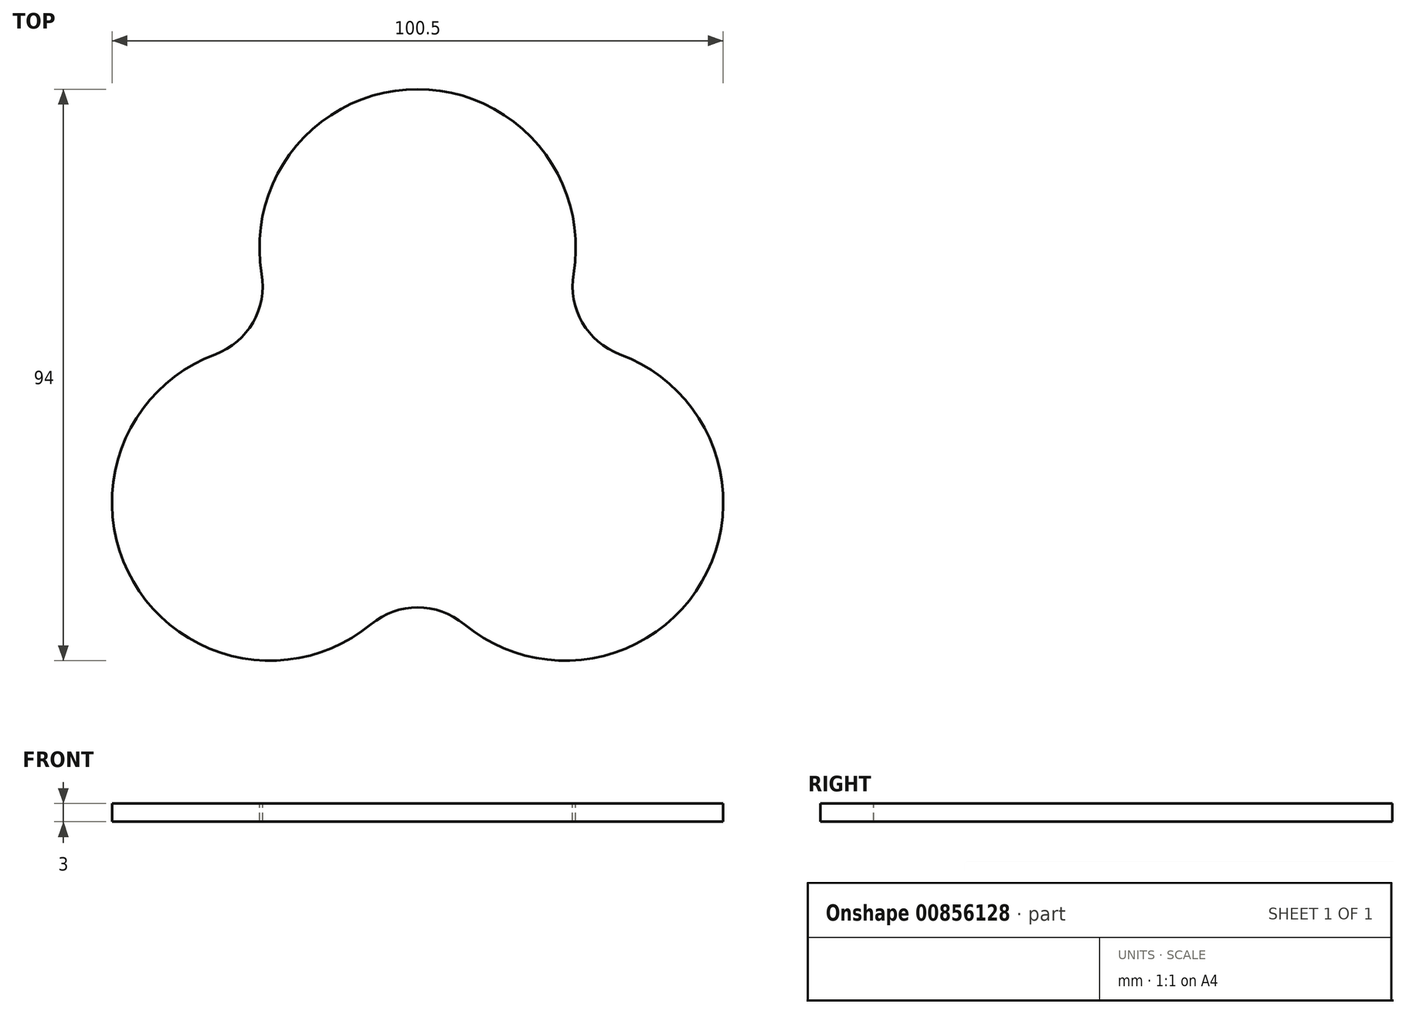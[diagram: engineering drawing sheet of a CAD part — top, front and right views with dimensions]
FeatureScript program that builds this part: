
annotation { "Feature Type Name" : "Feature", "Feature Type Description" : "" }
export const myFeature = defineFeature(function(context is Context, id is Id, definition is map)
    precondition{}
    {
        {
            var Q0;
            Q0=qCreatedBy(makeId("Top.planeOp"),FACE);
            var sketch = newSketch(context, id + "F0", { "sketchPlane" : qUnion([Q0])});
            skArc(sketch, "E0.0", {"start": v(25.25, 24.51) * mm, "mid": v(-0.38, 54.87) * mm, "end": v(-26.01, 24.51) * mm});
            skArc(sketch, "E1.0", {"start": v(-33.67, 11.25) * mm, "mid": v(-27.45, 16.5) * mm, "end": v(-26.01, 24.51) * mm});
            skArc(sketch, "E2.0", {"start": v(-33.67, 11.25) * mm, "mid": v(-47.15, -26.13) * mm, "end": v(-8.04, -33.15) * mm});
            skArc(sketch, "E3.0", {"start": v(7.28, -33.15) * mm, "mid": v(46.38, -26.13) * mm, "end": v(32.9, 11.25) * mm});
            skArc(sketch, "E4.0", {"start": v(7.28, -33.15) * mm, "mid": v(-0.38, -30.39) * mm, "end": v(-8.04, -33.15) * mm});
            skArc(sketch, "E5.0", {"start": v(25.25, 24.51) * mm, "mid": v(26.69, 16.5) * mm, "end": v(32.9, 11.25) * mm});
            skSolve(sketch);
        }
        {
            var Q0;
            Q0=makeQuery(id+"F0.imprint","IMPRINT",FACE,{"disambiguationData":[TD([[makeQuery(id+"F0.imprint","IMPRINT",EDGE,{"derivedFrom":sQuery(id+"F0.wireOp",EDGE,"E0.0")}),1.0]])]});
            extrude(context, id + "F1", {"entities" : qUnion([Q0]), "oppositeDirection" : true, "depth" : 3 * mm, "offsetDistance" : 25 * mm});
        }
    });
